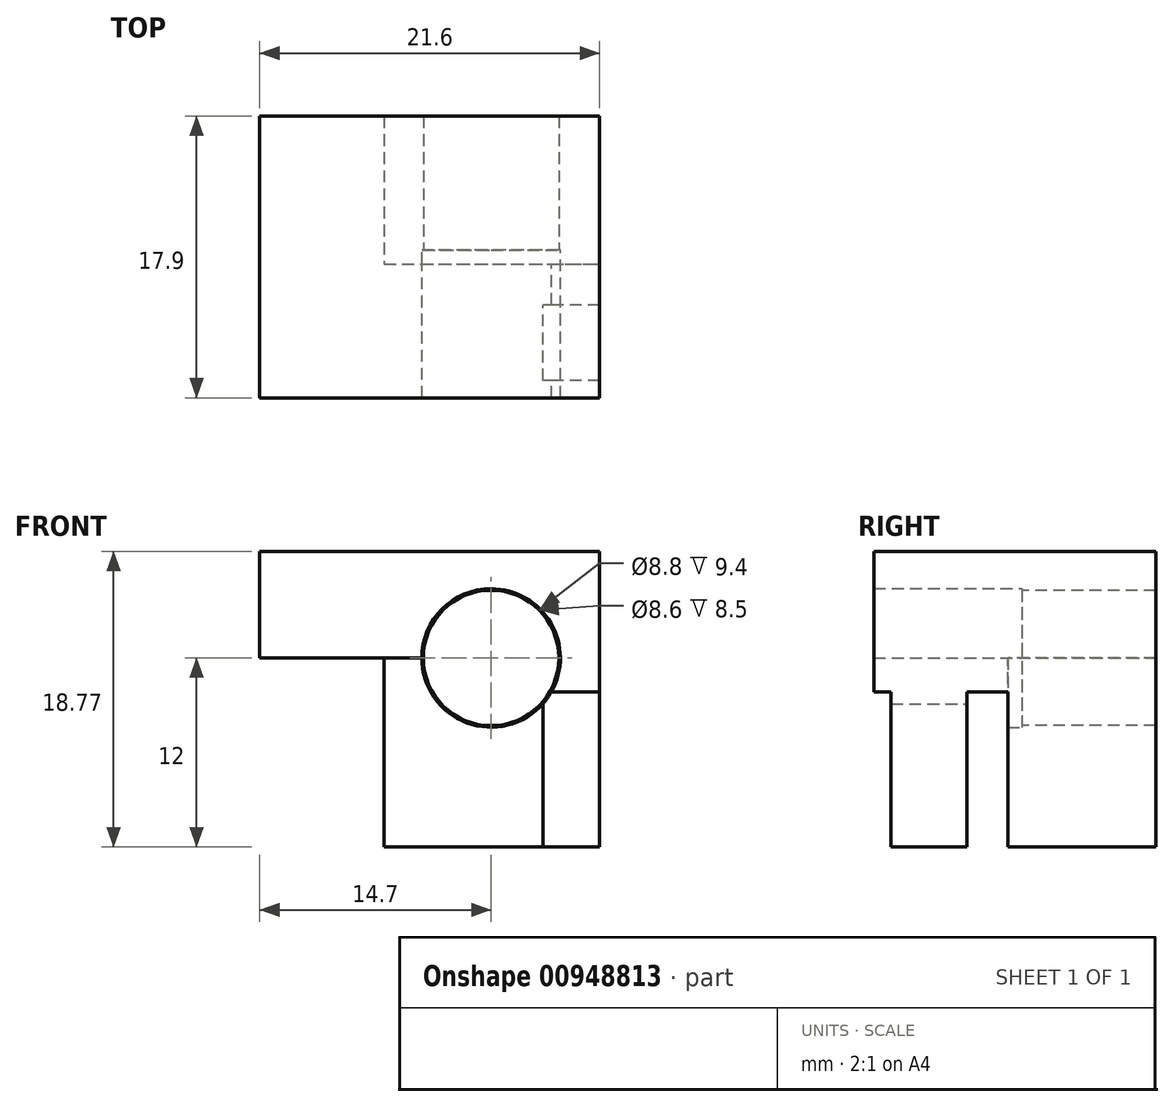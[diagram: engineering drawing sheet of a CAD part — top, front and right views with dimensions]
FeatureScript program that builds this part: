
annotation { "Feature Type Name" : "Feature", "Feature Type Description" : "" }
export const myFeature = defineFeature(function(context is Context, id is Id, definition is map)
    precondition{}
    {
        {
            assignVariable(context, id + "F0", {"name" : "T", "anyValue" : 0.9});
        }
        {
            assignVariable(context, id + "F1", {"name" : "R1", "anyValue" : 4.3});
        }
        {
            assignVariable(context, id + "F2", {"name" : "S", "anyValue" : 0.1});
        }
        {
            assignVariable(context, id + "F3", {"name" : "R2", "anyValue" : (11.75 / 2)});
        }
        {
            assignVariable(context, id + "F4", {"name" : "D", "anyValue" : 12});
        }
        {
            var Q0;
            Q0=qCreatedBy(makeId("Top.planeOp"),FACE);
            var sketch = newSketch(context, id + "F5", { "sketchPlane" : qUnion([Q0])});
            skLineSegment(sketch, "E0.bottom", {"start": v(-10.8, -4.25) * mm, "end": v(10.8, -4.25) * mm});
            skLineSegment(sketch, "E0.top", {"start": v(-10.8, 4.25) * mm, "end": v(10.8, 4.25) * mm});
            skLineSegment(sketch, "E0.left", {"start": v(-10.8, -4.25) * mm, "end": v(-10.8, 4.25) * mm});
            skLineSegment(sketch, "E0.right", {"start": v(10.8, -4.25) * mm, "end": v(10.8, 4.25) * mm});
            skPoint(sketch, "E0.middle", {"position": v(0, 0) * mm});
            skLineSegment(sketch, "E1.top", {"start": v(-10.8, 5.15) * mm, "end": v(10.8, 5.15) * mm});
            skLineSegment(sketch, "E1.left", {"start": v(-10.8, 4.25) * mm, "end": v(-10.8, 5.15) * mm});
            skLineSegment(sketch, "E1.right", {"start": v(10.8, 4.25) * mm, "end": v(10.8, 5.15) * mm});
            skLineSegment(sketch, "E2.bottom", {"start": v(10.8, 1.65) * mm, "end": v(7.2, 1.65) * mm});
            skLineSegment(sketch, "E2.top", {"start": v(10.8, -3.15) * mm, "end": v(7.2, -3.15) * mm});
            skLineSegment(sketch, "E2.left", {"start": v(10.8, 1.65) * mm, "end": v(10.8, -3.15) * mm});
            skLineSegment(sketch, "E2.right", {"start": v(7.2, 1.65) * mm, "end": v(7.2, -3.15) * mm});
            skLineSegment(sketch, "E3", {"start": v(-2.9, 5.15) * mm, "end": v(-2.9, 4.25) * mm});
            skLineSegment(sketch, "E4", {"start": v(3.9, 5.15) * mm, "end": v(3.9, -4.25) * mm, "construction": true});
            skSolve(sketch);
        }
        {
            var Q0;
            {var subQ0=sQuery(id+"F5.wireOp",EDGE,"E1.left");Q0=makeQuery(id+"F5.imprint","IMPRINT",FACE,{"disambiguationData":[TD([[makeQuery(id+"F5.imprint","IMPRINT",EDGE,{"derivedFrom":subQ0}),-1.0]])]});}
            var Q1;
            Q1=makeQuery(id+"F5.imprint","IMPRINT",FACE,{"disambiguationData":[TD([[makeQuery(id+"F5.imprint","IMPRINT",EDGE,{"derivedFrom":sQuery(id+"F5.wireOp",EDGE,"E2.bottom")}),1.0]])]});
            var Q2;
            {var subQ5=sQuery(id+"F5.wireOp",EDGE,"E0.bottom");Q2=makeQuery(id+"F5.imprint","IMPRINT",FACE,{"disambiguationData":[TD([[makeQuery(id+"F5.imprint","IMPRINT",EDGE,{"derivedFrom":subQ5}),1.0]])]});}
            var Q3;
            {var subQ0=sQuery(id+"F5.wireOp",EDGE,"E1.right");Q3=makeQuery(id+"F5.imprint","IMPRINT",FACE,{"disambiguationData":[TD([[makeQuery(id+"F5.imprint","IMPRINT",EDGE,{"derivedFrom":subQ0}),1.0]])]});}
            extrude(context, id + "F6", {"entities" : qUnion([Q0, Q1, Q2, Q3]), "depth" : (getVariable(context, 'R2') + getVariable(context, 'T')) * mm, "offsetDistance" : 25 * mm});
        }
        {
            var Q0;
            {var subQ0=sQuery(id+"F5.wireOp",EDGE,"E1.right");Q0=makeQuery(id+"F5.imprint","IMPRINT",FACE,{"disambiguationData":[TD([[makeQuery(id+"F5.imprint","IMPRINT",EDGE,{"derivedFrom":subQ0}),1.0]])]});}
            var Q1;
            Q1=makeQuery(id+"F5.imprint","IMPRINT",FACE,{"disambiguationData":[TD([[makeQuery(id+"F5.imprint","IMPRINT",EDGE,{"derivedFrom":sQuery(id+"F5.wireOp",EDGE,"E2.bottom")}),1.0]])]});
            extrude(context, id + "F7", {"entities" : qUnion([Q0, Q1]), "operationType" : NewBodyOperationType.ADD, "oppositeDirection" : true, "depth" : getVariable(context, 'D') * mm, "offsetDistance" : 25 * mm});
        }
        {
            var Q0;
            {var subQ0=sQuery(id+"F5.wireOp",EDGE,"E1.top");Q0=makeQuery(id+"F7.boolean.opBoolean","MERGE",FACE,{"derivedFrom":[makeQuery(id+"F6.opExtrude","SWEPT_FACE",FACE,{"disambiguationData":[OSD([subQ0])]}),makeQuery(id+"F7.opExtrude","SWEPT_FACE",FACE,{"disambiguationData":[OSD([subQ0])]})]});}
            var sketch = newSketch(context, id + "F8", { "sketchPlane" : qUnion([Q0])});
            skPoint(sketch, "E5.0", {"position": v(-3.9, 0) * mm});
            skCircle(sketch, "E6", {"center": v(-3.9, 0) * mm, "radius": 4.3 * mm});
            skCircle(sketch, "E7", {"center": v(-3.9, 0) * mm, "radius": 5.97 * mm});
            skSolve(sketch);
        }
        {
            var Q0;
            Q0=makeQuery(id+"F6.opExtrude","CAP_FACE",FACE,{"disambiguationData":[OSD([sQuery(id+"F5.wireOp",EDGE,"E0.bottom"),sQuery(id+"F5.wireOp",EDGE,"E0.left"),sQuery(id+"F5.wireOp",EDGE,"E0.right"),sQuery(id+"F5.wireOp",EDGE,"E1.top"),sQuery(id+"F5.wireOp",EDGE,"E1.left"),sQuery(id+"F5.wireOp",EDGE,"E1.right"),sQuery(id+"F5.wireOp",EDGE,"E2.left")])],"isStart":true});
            var sketch = newSketch(context, id + "F9", { "sketchPlane" : qUnion([Q0])});
            skLineSegment(sketch, "E8", {"start": v(3.95, -4.25) * mm, "end": v(3.95, 4.25) * mm});
            skSolve(sketch);
        }
        {
            var Q0;
            {var subQ2=sQuery(id+"F9.wireOp",EDGE,"E8");Q0=makeQuery(id+"F9.imprint","IMPRINT",FACE,{"disambiguationData":[TD([[makeQuery(id+"F9.imprint","IMPRINT",EDGE,{"derivedFrom":subQ2}),-1.0]])]});}
            extrude(context, id + "F10", {"entities" : qUnion([Q0]), "operationType" : NewBodyOperationType.ADD, "depth" : getVariable(context, 'R1') / 2 * mm, "offsetDistance" : 25 * mm});
        }
        {
            var Q0;
            Q0=sQuery(id+"F8.wireOp",VERTEX,"E5.0");
            var Q1;
            Q1=makeQuery(id+"F6.opExtrude","SWEPT_BODY",BODY,{"disambiguationData":[OSD([sQuery(id+"F5.wireOp",EDGE,"E0.bottom"),sQuery(id+"F5.wireOp",EDGE,"E0.left"),sQuery(id+"F5.wireOp",EDGE,"E0.right"),sQuery(id+"F5.wireOp",EDGE,"E1.top"),sQuery(id+"F5.wireOp",EDGE,"E1.left"),sQuery(id+"F5.wireOp",EDGE,"E1.right"),sQuery(id+"F5.wireOp",EDGE,"E2.left")])]});
            hole(context, id + "F11", {"style" : HoleStyle.SIMPLE, "endStyle" : HoleEndStyle.THROUGH, "holeDiameter" : 2 * (getVariable(context, 'R1') + getVariable(context, 'S')) * mm, "majorDiameter" : 5 * mm, "isTappedThrough" : true, "tappedDepth" : 12 * mm, "tapClearance" : 3, "locations" : qUnion([Q0]), "scope" : qUnion([Q1])});
        }
        {
            var Q0;
            Q0=makeQuery(id+"F8.imprint","IMPRINT",FACE,{"disambiguationData":[TD([[makeQuery(id+"F8.imprint","IMPRINT",EDGE,{"derivedFrom":sQuery(id+"F8.wireOp",EDGE,"E7")}),-1.0]])]});
            var Q1;
            Q1=makeQuery(id+"F8.imprint","IMPRINT",FACE,{"disambiguationData":[TD([[makeQuery(id+"F8.imprint","IMPRINT",EDGE,{"derivedFrom":sQuery(id+"F8.wireOp",EDGE,"E6")}),-1.0]])]});
            extrude(context, id + "F12", {"entities" : qUnion([Q0, Q1]), "operationType" : NewBodyOperationType.ADD, "depth" : 8.5 * mm, "offsetDistance" : 25 * mm});
        }
    });
